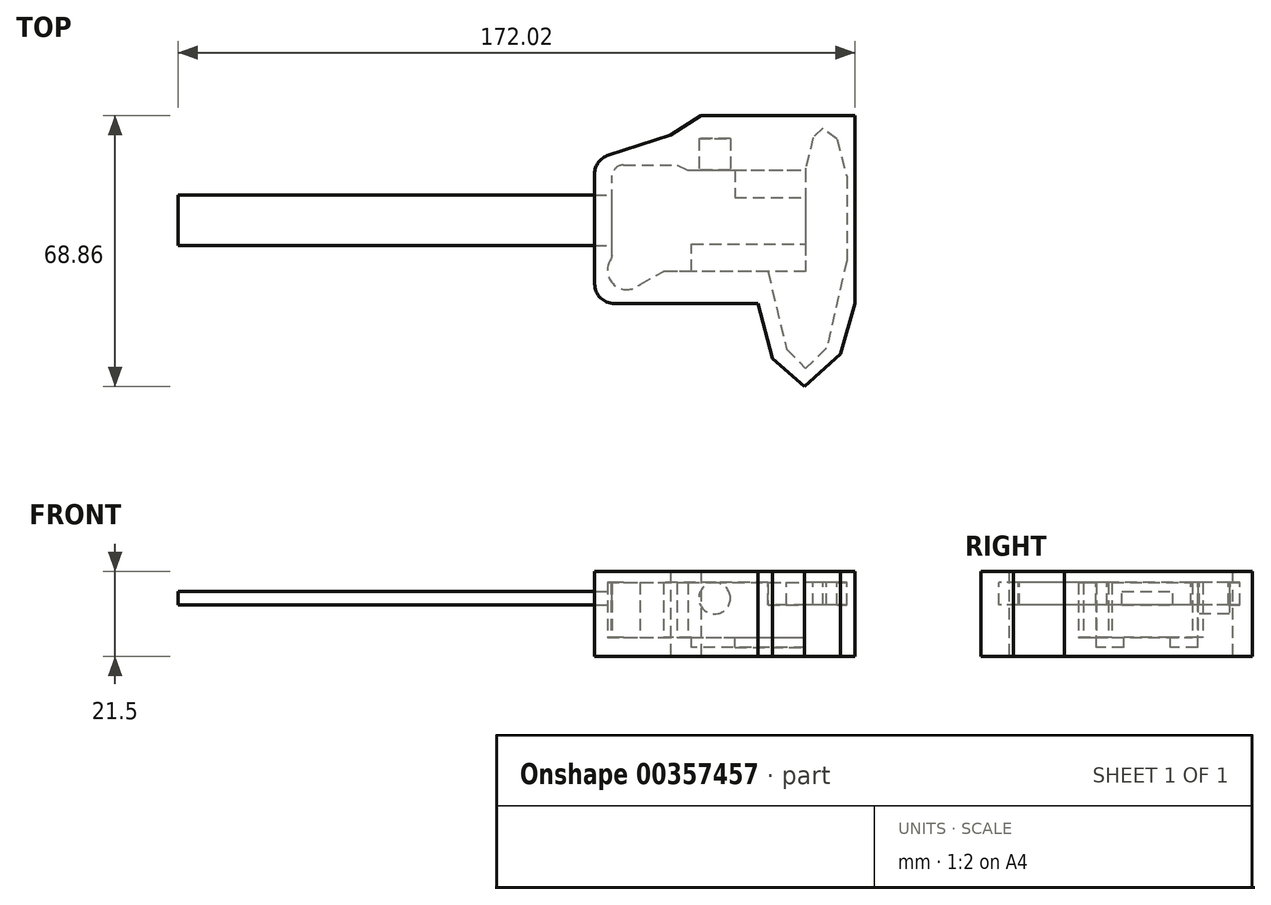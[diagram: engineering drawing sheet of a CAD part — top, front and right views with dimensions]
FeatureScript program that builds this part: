
annotation { "Feature Type Name" : "Feature", "Feature Type Description" : "" }
export const myFeature = defineFeature(function(context is Context, id is Id, definition is map)
    precondition{}
    {
        {
            var Q0;
            Q0=qCreatedBy(makeId("Top.planeOp"),FACE);
            var sketch = newSketch(context, id + "F0", { "sketchPlane" : qUnion([Q0])});
            skLineSegment(sketch, "E0", {"start": v(5.41, 29.06) * mm, "end": v(5.41, -45.98) * mm, "construction": true});
            skLineSegment(sketch, "E1", {"start": v(62.31, -3.71) * mm, "end": v(62.31, 29.06) * mm, "construction": true});
            skLineSegment(sketch, "E2", {"start": v(5.41, -8.46) * mm, "end": v(-121.38, -8.46) * mm, "construction": true});
            skSolve(sketch);
        }
        {
            var Q0;
            Q0=qCreatedBy(makeId("Top.planeOp"),FACE);
            var sketch = newSketch(context, id + "F1", { "sketchPlane" : qUnion([Q0])});
            skLineSegment(sketch, "E3.bottom", {"start": v(-107.5, -8.55) * mm, "end": v(5.4, -8.55) * mm});
            skLineSegment(sketch, "E3.top", {"start": v(-107.5, 4.28) * mm, "end": v(5.4, 4.28) * mm});
            skLineSegment(sketch, "E3.left", {"start": v(-107.5, -8.55) * mm, "end": v(-107.5, 4.28) * mm});
            skLineSegment(sketch, "E3.right", {"start": v(5.4, -8.55) * mm, "end": v(5.4, 4.28) * mm});
            skLineSegment(sketch, "E4", {"start": v(42.37, -15.19) * mm, "end": v(47.1, -34.87) * mm});
            skLineSegment(sketch, "E5", {"start": v(47.1, -34.87) * mm, "end": v(51.63, -39.5) * mm});
            skLineSegment(sketch, "E6", {"start": v(62.37, 8.96) * mm, "end": v(62.37, -12.39) * mm});
            skLineSegment(sketch, "E7", {"start": v(62.37, -12.39) * mm, "end": v(57.24, -34.59) * mm});
            skLineSegment(sketch, "E8", {"start": v(57.24, -34.59) * mm, "end": v(51.92, -39.8) * mm});
            skLineSegment(sketch, "E9", {"start": v(51.63, -39.5) * mm, "end": v(51.92, -39.8) * mm});
            skLineSegment(sketch, "E10", {"start": v(59.87, 18.47) * mm, "end": v(62.37, 8.96) * mm});
            skLineSegment(sketch, "E11", {"start": v(59.87, 18.47) * mm, "end": v(56.36, 21.31) * mm});
            skLineSegment(sketch, "E12", {"start": v(56.36, 21.31) * mm, "end": v(53.85, 18.95) * mm});
            skLineSegment(sketch, "E13", {"start": v(53.85, 18.95) * mm, "end": v(51.86, 11.12) * mm});
            skLineSegment(sketch, "E14", {"start": v(51.86, 11.12) * mm, "end": v(51.86, -4.74) * mm});
            skLineSegment(sketch, "E15", {"start": v(51.86, -4.74) * mm, "end": v(49.17, -4.74) * mm});
            skLineSegment(sketch, "E16", {"start": v(49.17, -4.74) * mm, "end": v(49.17, -12.95) * mm});
            skLineSegment(sketch, "E17", {"start": v(49.17, -12.95) * mm, "end": v(42.31, -13) * mm});
            skLineSegment(sketch, "E18", {"start": v(42.31, -13) * mm, "end": v(42.37, -15.19) * mm});
            skSolve(sketch);
        }
        {
            var Q0;
            Q0 = qSketchRegion(id + "F1", true);
            extrude(context, id + "F2", {"entities" : qUnion([Q0]), "oppositeDirection" : true, "depth" : 3.5 * mm});
        }
        {
            var Q0;
            Q0=qCreatedBy(makeId("Top.planeOp"),FACE);
            var sketch = newSketch(context, id + "F3", { "sketchPlane" : qUnion([Q0])});
            skLineSegment(sketch, "E19", {"start": v(2.78, -11.1) * mm, "end": v(2.78, 9.27) * mm});
            skLineSegment(sketch, "E20", {"start": v(5.7, 11.97) * mm, "end": v(19.25, 11.97) * mm});
            skLineSegment(sketch, "E21", {"start": v(22, 10.65) * mm, "end": v(56.27, 10.65) * mm});
            skLineSegment(sketch, "E22", {"start": v(56.27, 10.65) * mm, "end": v(56.27, 21.5) * mm});
            skLineSegment(sketch, "E23.0", {"start": v(59.87, 18.47) * mm, "end": v(56.36, 21.31) * mm});
            skLineSegment(sketch, "E23.1", {"start": v(59.87, 18.47) * mm, "end": v(62.37, 8.96) * mm});
            skLineSegment(sketch, "E24", {"start": v(62.37, 8.96) * mm, "end": v(62.37, -4.76) * mm});
            skLineSegment(sketch, "E25", {"start": v(62.37, -4.76) * mm, "end": v(51.92, -4.76) * mm});
            skLineSegment(sketch, "E26", {"start": v(51.92, -4.76) * mm, "end": v(51.92, -15.1) * mm});
            skLineSegment(sketch, "E27", {"start": v(51.92, -15.1) * mm, "end": v(15.77, -15.1) * mm});
            skArc(sketch, "E28", {"start": v(2.43, -11.99) * mm, "mid": v(3.29, -18.5) * mm, "end": v(9.86, -18.44) * mm});
            skLineSegment(sketch, "E29", {"start": v(9.86, -18.44) * mm, "end": v(15.77, -15.1) * mm});
            skLineSegment(sketch, "E30", {"start": v(2.78, -11.1) * mm, "end": v(2.43, -11.99) * mm});
            skArc(sketch, "E31", {"start": v(5.7, 11.97) * mm, "mid": v(3.72, 11.2) * mm, "end": v(2.78, 9.27) * mm});
            skLineSegment(sketch, "E32", {"start": v(19.25, 11.97) * mm, "end": v(22, 10.65) * mm});
            skLineSegment(sketch, "E33", {"start": v(51.92, -4.76) * mm, "end": v(51.92, 10.65) * mm});
            skSolve(sketch);
        }
        {
            var Q0;
            Q0=makeQuery(id+"F3.imprint","IMPRINT",FACE,{"disambiguationData":[TD([[makeQuery(id+"F3.imprint","IMPRINT",EDGE,{"derivedFrom":sQuery(id+"F3.wireOp",EDGE,"E19")}),-1.0]])]});
            var Q1;
            Q1=makeQuery(id+"F2.opExtrude","CAP_FACE",FACE,{"disambiguationData":[OSD([sQuery(id+"F1.wireOp",EDGE,"E4"),sQuery(id+"F1.wireOp",EDGE,"E5"),sQuery(id+"F1.wireOp",EDGE,"E6"),sQuery(id+"F1.wireOp",EDGE,"E7"),sQuery(id+"F1.wireOp",EDGE,"E8"),sQuery(id+"F1.wireOp",EDGE,"E9"),sQuery(id+"F1.wireOp",EDGE,"E10"),sQuery(id+"F1.wireOp",EDGE,"E11"),sQuery(id+"F1.wireOp",EDGE,"E12"),sQuery(id+"F1.wireOp",EDGE,"E13"),sQuery(id+"F1.wireOp",EDGE,"E14"),sQuery(id+"F1.wireOp",EDGE,"E15"),sQuery(id+"F1.wireOp",EDGE,"E16"),sQuery(id+"F1.wireOp",EDGE,"E17"),sQuery(id+"F1.wireOp",EDGE,"E18")])],"isStart":true});
            extrude(context, id + "F4", {"entities" : qUnion([Q0, Q1]), "operationType" : NewBodyOperationType.ADD, "depth" : 2.25 * mm});
        }
        {
            var Q0;
            Q0=makeQuery(id+"F3.imprint","IMPRINT",FACE,{"disambiguationData":[TD([[makeQuery(id+"F3.imprint","IMPRINT",EDGE,{"derivedFrom":sQuery(id+"F3.wireOp",EDGE,"E19")}),-1.0]])]});
            extrude(context, id + "F5", {"entities" : qUnion([Q0]), "operationType" : NewBodyOperationType.ADD, "oppositeDirection" : true, "depth" : 8.5 * mm + 3.25 * mm});
        }
        {
            var Q0;
            {var subQ0=sQuery(id+"F3.wireOp",EDGE,"E21");Q0=makeQuery(id+"F5.boolean.opBoolean","MERGE",FACE,{"derivedFrom":[makeQuery(id+"F4.opExtrude","SWEPT_FACE",FACE,{"disambiguationData":[OSD([subQ0])]}),makeQuery(id+"F5.opExtrude","SWEPT_FACE",FACE,{"disambiguationData":[OSD([subQ0])]})]});}
            var sketch = newSketch(context, id + "F6", { "sketchPlane" : qUnion([Q0])});
            skLineSegment(sketch, "E34", {"start": v(1.23, -1.75) * mm, "end": v(-45.56, -1.75) * mm, "construction": true});
            skLineSegment(sketch, "E35", {"start": v(-28.8, -1.75) * mm, "end": v(-28.8, -11.75) * mm, "construction": true});
            skCircle(sketch, "E36", {"center": v(-28.8, -1.75) * mm, "radius": 4 * mm});
            skSolve(sketch);
        }
        {
            var Q0;
            Q0 = qSketchRegion(id + "F6", true);
            extrude(context, id + "F7", {"entities" : qUnion([Q0]), "operationType" : NewBodyOperationType.ADD, "depth" : 8 * mm});
        }
        {
            var Q0;
            Q0=makeQuery(id+"F5.opExtrude","CAP_FACE",FACE,{"disambiguationData":[OSD([sQuery(id+"F1.wireOp",EDGE,"E4"),sQuery(id+"F1.wireOp",EDGE,"E5"),sQuery(id+"F1.wireOp",EDGE,"E6"),sQuery(id+"F1.wireOp",EDGE,"E7"),sQuery(id+"F1.wireOp",EDGE,"E8"),sQuery(id+"F1.wireOp",EDGE,"E9"),sQuery(id+"F1.wireOp",EDGE,"E10"),sQuery(id+"F1.wireOp",EDGE,"E11"),sQuery(id+"F1.wireOp",EDGE,"E12"),sQuery(id+"F1.wireOp",EDGE,"E13"),sQuery(id+"F1.wireOp",EDGE,"E14"),sQuery(id+"F1.wireOp",EDGE,"E15"),sQuery(id+"F1.wireOp",EDGE,"E16"),sQuery(id+"F1.wireOp",EDGE,"E17"),sQuery(id+"F1.wireOp",EDGE,"E18"),sQuery(id+"F3.wireOp",EDGE,"E19"),sQuery(id+"F3.wireOp",EDGE,"E20"),sQuery(id+"F3.wireOp",EDGE,"E21"),sQuery(id+"F3.wireOp",EDGE,"E26"),sQuery(id+"F3.wireOp",EDGE,"E27"),sQuery(id+"F3.wireOp",EDGE,"E28"),sQuery(id+"F3.wireOp",EDGE,"E29"),sQuery(id+"F3.wireOp",EDGE,"E30"),sQuery(id+"F3.wireOp",EDGE,"E31"),sQuery(id+"F3.wireOp",EDGE,"E32"),sQuery(id+"F3.wireOp",EDGE,"E33")])],"isStart":false});
            var sketch = newSketch(context, id + "F8", { "sketchPlane" : qUnion([Q0])});
            skLineSegment(sketch, "E37.bottom", {"start": v(22.92, 15.1) * mm, "end": v(51.92, 15.1) * mm});
            skLineSegment(sketch, "E37.top", {"start": v(22.92, 8.1) * mm, "end": v(51.92, 8.1) * mm});
            skLineSegment(sketch, "E37.left", {"start": v(22.92, 15.1) * mm, "end": v(22.92, 8.1) * mm});
            skLineSegment(sketch, "E37.right", {"start": v(51.92, 15.1) * mm, "end": v(51.92, 8.1) * mm});
            skLineSegment(sketch, "E38.bottom", {"start": v(33.92, -10.65) * mm, "end": v(51.92, -10.65) * mm});
            skLineSegment(sketch, "E38.top", {"start": v(33.92, -3.65) * mm, "end": v(51.92, -3.65) * mm});
            skLineSegment(sketch, "E38.left", {"start": v(33.92, -10.65) * mm, "end": v(33.92, -3.65) * mm});
            skLineSegment(sketch, "E38.right", {"start": v(51.92, -10.65) * mm, "end": v(51.92, -3.65) * mm});
            skSolve(sketch);
        }
        {
            var Q0;
            Q0 = qSketchRegion(id + "F8", true);
            extrude(context, id + "F9", {"entities" : qUnion([Q0]), "operationType" : NewBodyOperationType.ADD, "depth" : 2.5 * mm});
        }
        {
            var Q0;
            Q0=qCreatedBy(makeId("Top.planeOp"),FACE);
            var sketch = newSketch(context, id + "F10", { "sketchPlane" : qUnion([Q0])});
            skLineSegment(sketch, "E39.bottom", {"start": v(64.5, 24.48) * mm, "end": v(25.36, 24.48) * mm});
            skLineSegment(sketch, "E39.top", {"start": v(39.88, -23.27) * mm, "end": v(3.34, -23.27) * mm});
            skLineSegment(sketch, "E39.left", {"start": v(64.5, 24.48) * mm, "end": v(64.5, -23.27) * mm});
            skLineSegment(sketch, "E39.right", {"start": v(-1.66, 9.68) * mm, "end": v(-1.66, -18.27) * mm});
            skLineSegment(sketch, "E40", {"start": v(39.88, -23.27) * mm, "end": v(43.44, -37.27) * mm});
            skLineSegment(sketch, "E41", {"start": v(43.44, -37.27) * mm, "end": v(51.59, -44.38) * mm});
            skLineSegment(sketch, "E42", {"start": v(51.59, -44.38) * mm, "end": v(60.77, -36.12) * mm});
            skLineSegment(sketch, "E43", {"start": v(60.77, -36.12) * mm, "end": v(64.5, -23.27) * mm});
            skLineSegment(sketch, "E44", {"start": v(1.81, 14.44) * mm, "end": v(17.64, 19.5) * mm});
            skLineSegment(sketch, "E45", {"start": v(17.64, 19.5) * mm, "end": v(25.36, 24.48) * mm});
            skPoint(sketch, "E46.visualSharp", {"position": v(-1.66, 13.33) * mm});
            skArc(sketch, "E46.filletArc", {"start": v(1.81, 14.44) * mm, "mid": v(-0.7, 12.63) * mm, "end": v(-1.66, 9.68) * mm});
            skPoint(sketch, "E47.visualSharp", {"position": v(-1.66, -23.27) * mm});
            skArc(sketch, "E47.filletArc", {"start": v(-1.66, -18.27) * mm, "mid": v(-0.2, -21.8) * mm, "end": v(3.34, -23.27) * mm});
            skSolve(sketch);
        }
        {
            var Q0;
            Q0 = qSketchRegion(id + "F10", true);
            extrude(context, id + "F11", {"entities" : qUnion([Q0]), "depth" : 5 * mm, "hasSecondDirection" : true, "secondDirectionOppositeDirection" : true, "secondDirectionDepth" : 16.5 * mm});
        }
    });
